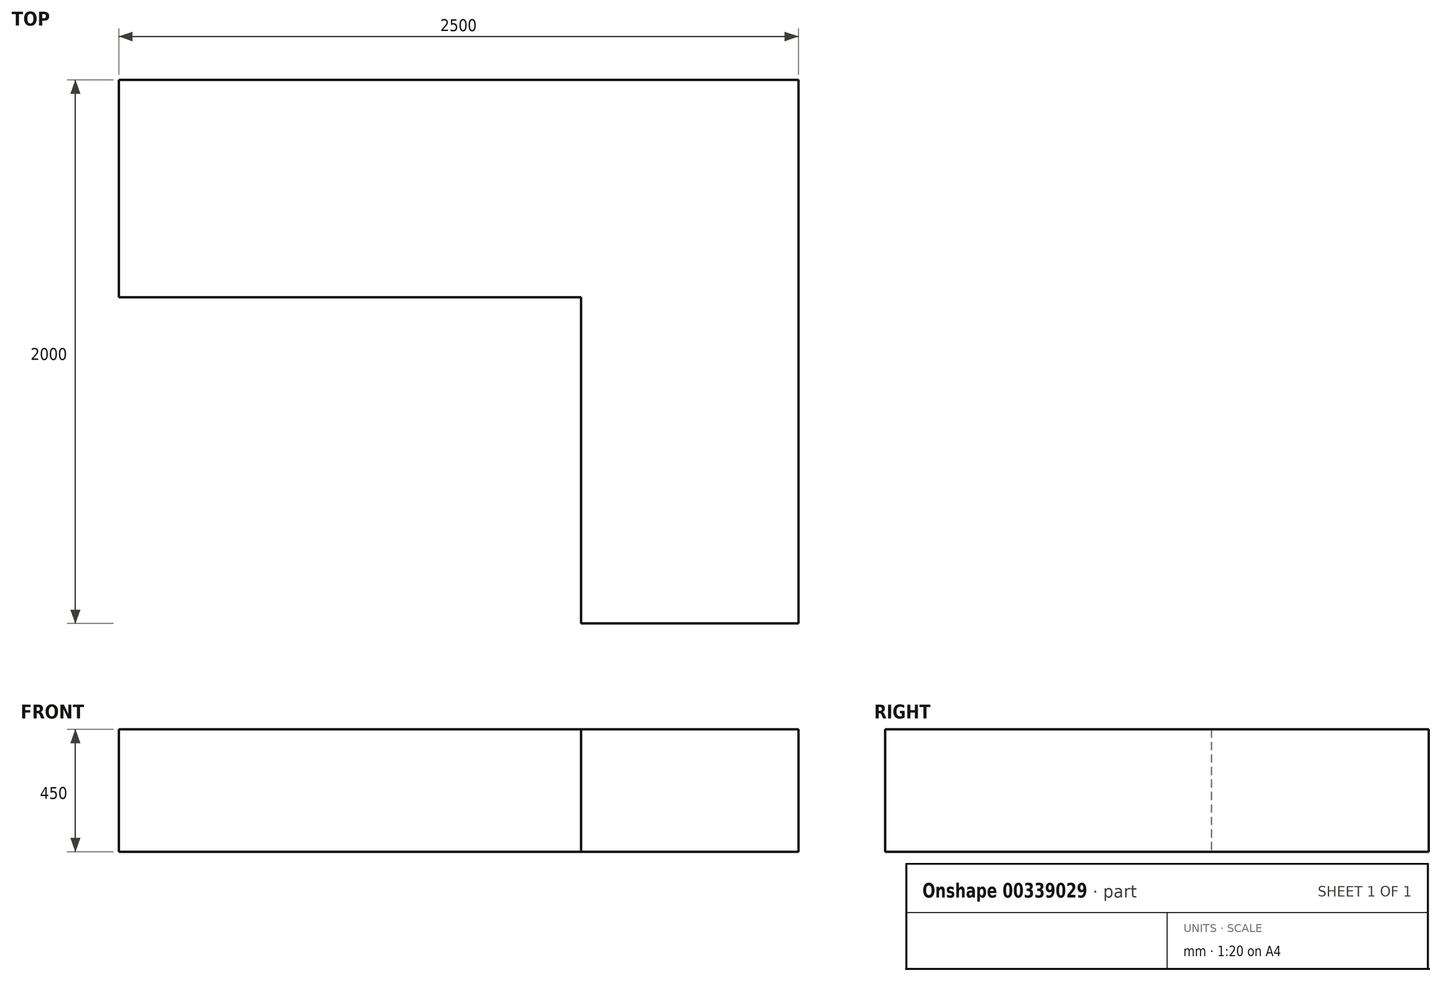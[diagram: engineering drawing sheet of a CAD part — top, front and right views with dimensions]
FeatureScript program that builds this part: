
annotation { "Feature Type Name" : "Feature", "Feature Type Description" : "" }
export const myFeature = defineFeature(function(context is Context, id is Id, definition is map)
    precondition{}
    {
        {
            var Q0;
            Q0=qCreatedBy(makeId("Top.planeOp"),FACE);
            var sketch = newSketch(context, id + "F0", { "sketchPlane" : qUnion([Q0])});
            skLineSegment(sketch, "E0", {"start": v(0, 0) * mm, "end": v(0, -1200) * mm});
            skLineSegment(sketch, "E1", {"start": v(0, -1200) * mm, "end": v(800, -1200) * mm});
            skLineSegment(sketch, "E2", {"start": v(800, -1200) * mm, "end": v(800, 800) * mm});
            skLineSegment(sketch, "E3", {"start": v(800, 800) * mm, "end": v(-1700, 800) * mm});
            skLineSegment(sketch, "E4", {"start": v(-1700, 800) * mm, "end": v(-1700, 0) * mm});
            skLineSegment(sketch, "E5", {"start": v(-1700, 0) * mm, "end": v(0, 0) * mm});
            skSolve(sketch);
        }
        {
            var Q0;
            Q0 = qSketchRegion(id + "F0", true);
            extrude(context, id + "F1", {"entities" : qUnion([Q0]), "depth" : 450 * mm});
        }
    });
